# Revit family: Accessory-Grab_Bar-KOHLER-Contemporary-K-14565
name_source: partatom
category: Specialty Equipment
revit_build: Autodesk Revit 2015 (Build: 20140606_1530(x64)
units: mm (PartAtom-declared; Revit-internal decimal feet)

## types (4) — shared parameters
ADA Compliant = Yes
Assembly Code = C1030200
Date Modified = 02/27/2019
Default Elevation = 42"
Description = 42 Inch Grab Bar
Height = 2 13/16"
Length = 42"
Manufacturer = KOHLER Co.
MasterFormat 1995 = 10820
MasterFormat 2004 = 10.28.13
Material = Premium Metal Construction
Product Documentation Link = https://www.us.kohler.com
Product Name = Contemporary
Product Page URL = http://www.us.kohler.com
URL = https://www.us.kohler.com
WaterSense Certified = No
Width = 2 3/4"

## per-type parameters (varying)
| type | Finish | Model | Type |
| S-Polished Stainless | Kohler-Metal-S-Polished_Stainless | K-14565-S | 1 |
| BN-Vibrant Brushed Nickel | Kohler-Metal-BN-Vibrant_Brushed_Nickel | K-14565-BN | 2 |
| BS-Brushed Stainless | Kohler-Metal-BS-Brushed_Stainless | K-14565-BS | 3 |
| TT-Titanium | Kohler-Metal-TT-Vibrant_Titanium | K-14565-TT | 4 |

## geometry (parser evidence)
native form markers: Sweep x7
no freeform markers — native parametric forms only
